# Revit family: QF_TRUE_STR1RPT-1G-1G-HC
name_source: partatom
category: Specialty Equipment
revit_build: Autodesk Revit Architecture 2012 (Build: 20110916_2132(x64)
units: mm (PartAtom-declared; Revit-internal decimal feet)

## types (1)
- QF_TRUE_STR1RPT-1G-1G-HC
    Apparent Power = 437 VA
    Conn Conduit = Yes
    Conn Plug = 5-15P
    Cycle = 60 Hz
    Depth = 36 1/8"
    Description = PASS-THRU GLASS FRONT/GLASS REAR SWING DOORS REFRIGERATOR WITH HYDROCARBON REFRIGERANT
    FL Amps = 4 A
    HP = 1/4
    Height = 77 3/4"
    Length = 27 1/2"
    Manufacturer = TRUE FOOD SERVICE EQUIPMENT, INC.
    Max Overcurrent Protection = 4 A
    Min Ckt Ampacity = 4 A
    Model = STR1RPT-1G-1G-HC
    Phase = 1
    Type Comments = www.truemfg.com
    URL = www.truemfg.com
    URL Cutsheet = www.truemfg.com
    URL Manufacturer = www.truemfg.com
    Volts = 115 V
    Watts = 437 W
    Weight in Pounds = 0

## geometry (parser evidence)
native form markers: Blend x8, Sweep x2
no freeform markers — native parametric forms only
